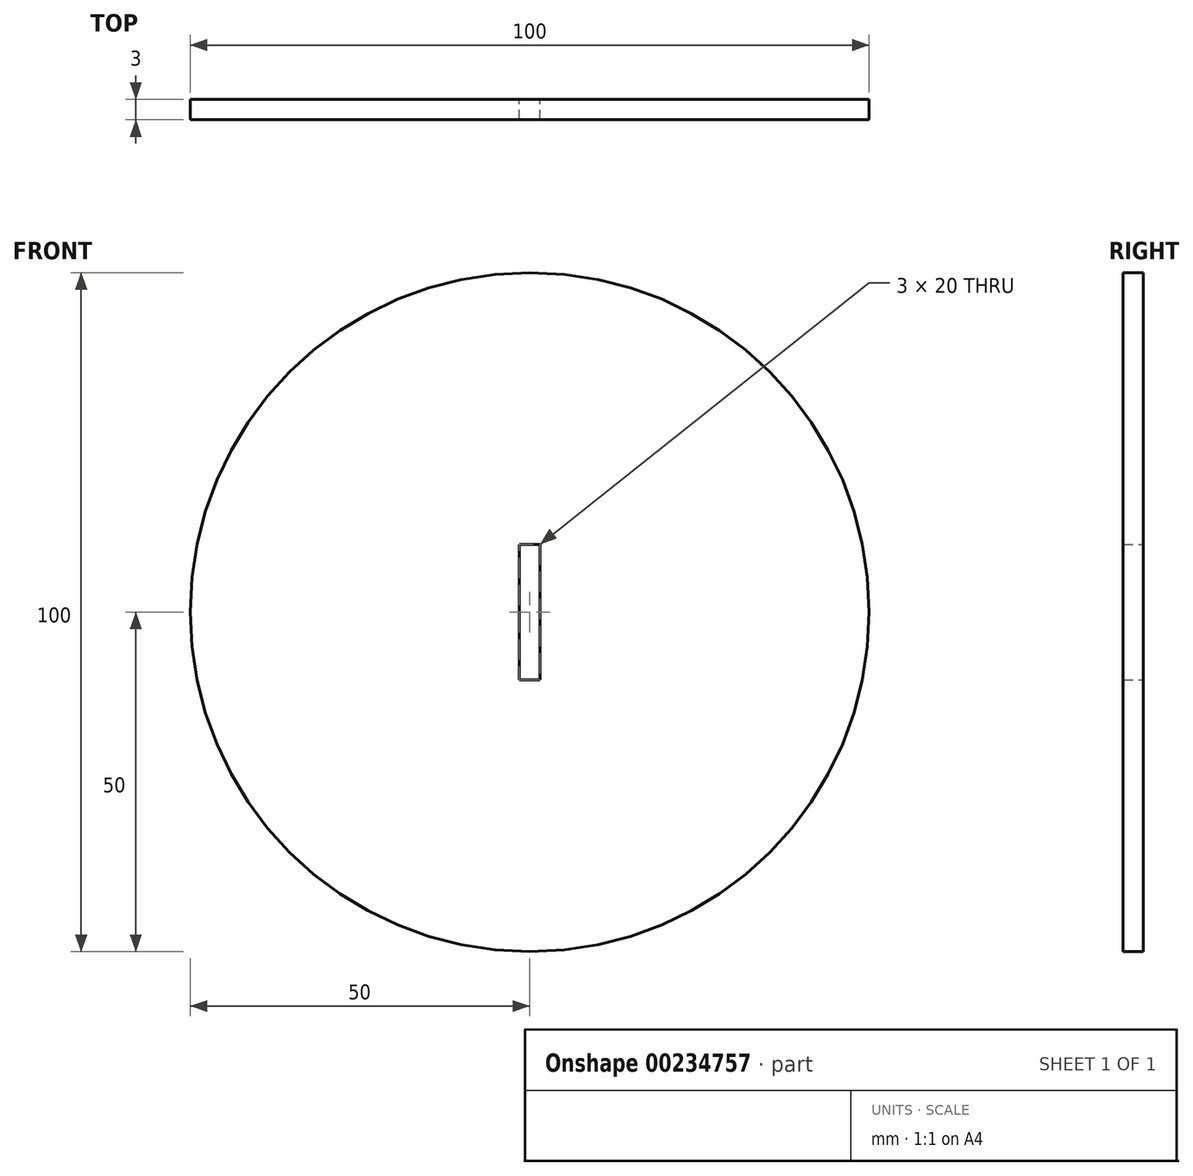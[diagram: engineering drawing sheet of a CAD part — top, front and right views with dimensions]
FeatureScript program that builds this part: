
annotation { "Feature Type Name" : "Feature", "Feature Type Description" : "" }
export const myFeature = defineFeature(function(context is Context, id is Id, definition is map)
    precondition{}
    {
        {
            var Q0;
            Q0=qCreatedBy(makeId("Front.planeOp"),FACE);
            var sketch = newSketch(context, id + "F0", { "sketchPlane" : qUnion([Q0])});
            skCircle(sketch, "E0", {"center": v(0, 0) * mm, "radius": 50 * mm});
            skLineSegment(sketch, "E1.bottom", {"start": v(-1.5, 10) * mm, "end": v(1.5, 10) * mm});
            skLineSegment(sketch, "E1.top", {"start": v(-1.5, -10) * mm, "end": v(1.5, -10) * mm});
            skLineSegment(sketch, "E1.left", {"start": v(-1.5, 10) * mm, "end": v(-1.5, -10) * mm});
            skLineSegment(sketch, "E1.right", {"start": v(1.5, 10) * mm, "end": v(1.5, -10) * mm});
            skSolve(sketch);
        }
        {
            var Q0;
            Q0=makeQuery(id+"F0.imprint","IMPRINT",FACE,{"disambiguationData":[TD([[makeQuery(id+"F0.imprint","IMPRINT",EDGE,{"derivedFrom":sQuery(id+"F0.wireOp",EDGE,"E0")}),1.0]])]});
            extrude(context, id + "F1", {"entities" : qUnion([Q0]), "depth" : 3 * mm});
        }
    });
